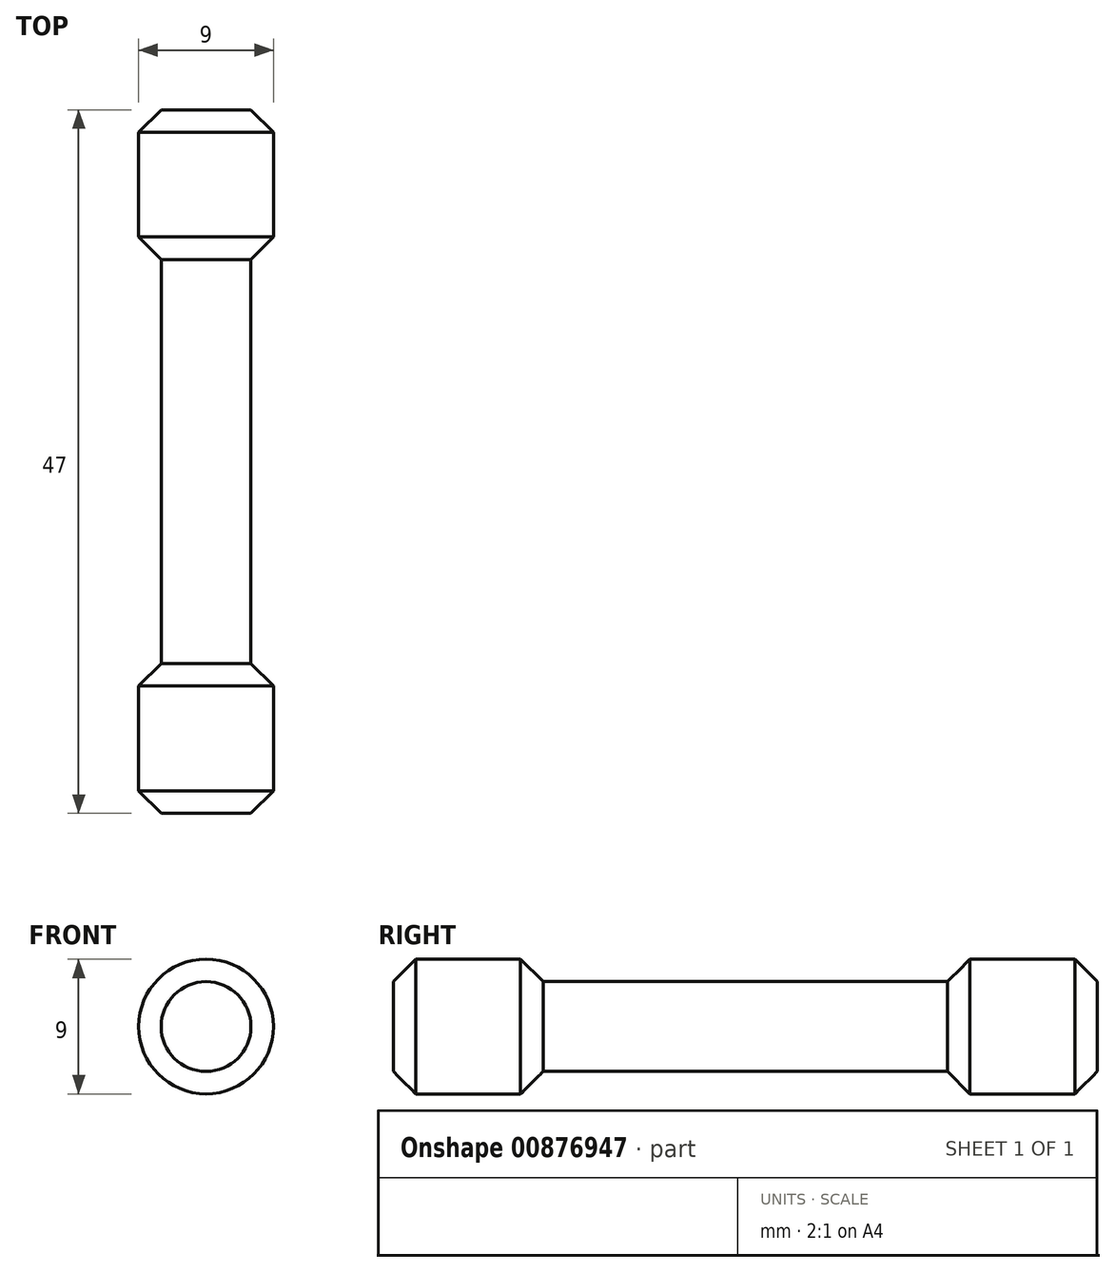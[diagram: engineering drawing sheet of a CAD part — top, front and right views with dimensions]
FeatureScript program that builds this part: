
annotation { "Feature Type Name" : "Feature", "Feature Type Description" : "" }
export const myFeature = defineFeature(function(context is Context, id is Id, definition is map)
    precondition{}
    {
        {
            var Q0;
            Q0=qCreatedBy(makeId("Front.planeOp"),FACE);
            var sketch = newSketch(context, id + "F0", { "sketchPlane" : qUnion([Q0])});
            skCircle(sketch, "E0", {"center": v(0, 0) * mm, "radius": 3 * mm});
            skSolve(sketch);
        }
        {
            var Q0;
            Q0 = qSketchRegion(id + "F0", true);
            extrude(context, id + "F1", {"entities" : qUnion([Q0]), "depth" : 47 * mm, "offsetDistance" : 25 * mm});
        }
        {
            var Q0;
            Q0=makeQuery(id+"F1.opExtrude","CAP_FACE",FACE,{"disambiguationData":[OSD([sQuery(id+"F0.wireOp",EDGE,"E0")])],"isStart":false});
            var sketch = newSketch(context, id + "F2", { "sketchPlane" : qUnion([Q0])});
            skCircle(sketch, "E1", {"center": v(0, 0) * mm, "radius": 4.5 * mm});
            skSolve(sketch);
        }
        {
            var Q0;
            Q0=makeQuery(id+"F2.imprint","IMPRINT",FACE,{"disambiguationData":[TD([[makeQuery(id+"F2.imprint","IMPRINT",EDGE,{"derivedFrom":sQuery(id+"F2.wireOp",EDGE,"E1")}),1.0]])]});
            extrude(context, id + "F3", {"entities" : qUnion([Q0]), "operationType" : NewBodyOperationType.ADD, "oppositeDirection" : true, "depth" : 10 * mm, "offsetDistance" : 25 * mm});
        }
        {
            var Q0;
            Q0=makeQuery(id+"F3.opExtrude","CAP_EDGE",EDGE,{"disambiguationData":[OSD([sQuery(id+"F2.wireOp",EDGE,"E1")])],"isStart":false});
            var Q1;
            Q1=makeQuery(id+"F3.opExtrude","CAP_EDGE",EDGE,{"disambiguationData":[OSD([sQuery(id+"F2.wireOp",EDGE,"E1")])],"isStart":true});
            chamfer(context, id + "F4", {"entities" : qUnion([Q0, Q1]), "width" : 1.5 * mm, "tangentPropagation" : true});
        }
        {
            var Q0;
            Q0=makeQuery(id+"F1.opExtrude","CAP_FACE",FACE,{"disambiguationData":[OSD([sQuery(id+"F0.wireOp",EDGE,"E0")])],"isStart":true});
            var sketch = newSketch(context, id + "F5", { "sketchPlane" : qUnion([Q0])});
            skCircle(sketch, "E2", {"center": v(0, 0) * mm, "radius": 4.5 * mm});
            skSolve(sketch);
        }
        {
            var Q0;
            Q0 = qSketchRegion(id + "F5", true);
            extrude(context, id + "F6", {"entities" : qUnion([Q0]), "operationType" : NewBodyOperationType.ADD, "oppositeDirection" : true, "depth" : 10 * mm, "offsetDistance" : 25 * mm});
        }
        {
            var Q0;
            Q0=makeQuery(id+"F6.opExtrude","CAP_EDGE",EDGE,{"disambiguationData":[OSD([sQuery(id+"F5.wireOp",EDGE,"E2")])],"isStart":false});
            var Q1;
            Q1=makeQuery(id+"F6.opExtrude","CAP_EDGE",EDGE,{"disambiguationData":[OSD([sQuery(id+"F5.wireOp",EDGE,"E2")])],"isStart":true});
            chamfer(context, id + "F7", {"entities" : qUnion([Q0, Q1]), "width" : 1.5 * mm, "tangentPropagation" : true});
        }
        {
            var Q0;
            Q0=qCreatedBy(makeId("Top.planeOp"),FACE);
            var sketch = newSketch(context, id + "F8", { "sketchPlane" : qUnion([Q0])});
            skLineSegment(sketch, "E3", {"start": v(-6.2, -22) * mm, "end": v(7.16, -22) * mm});
            skSolve(sketch);
        }
        {
            var Q0;
            Q0 = qSketchRegion(id + "F8", true);
            var Q1;
            Q1=sQuery(id+"F8.wireOp",EDGE,"E3");
            extrude(context, id + "F9", {"entities" : qUnion([Q0]), "bodyType" : ToolBodyType.SURFACE, "surfaceEntities" : qUnion([Q1]), "depth" : 25 * mm, "offsetDistance" : 25 * mm});
        }
        {
            var Q0;
            Q0=makeQuery(id+"F9.opExtrude","SWEPT_FACE",FACE,{"disambiguationData":[OSD([sQuery(id+"F8.wireOp",EDGE,"E3")])]});
            var sketch = newSketch(context, id + "F10", { "sketchPlane" : qUnion([Q0])});
            skSolve(sketch);
        }
    });
